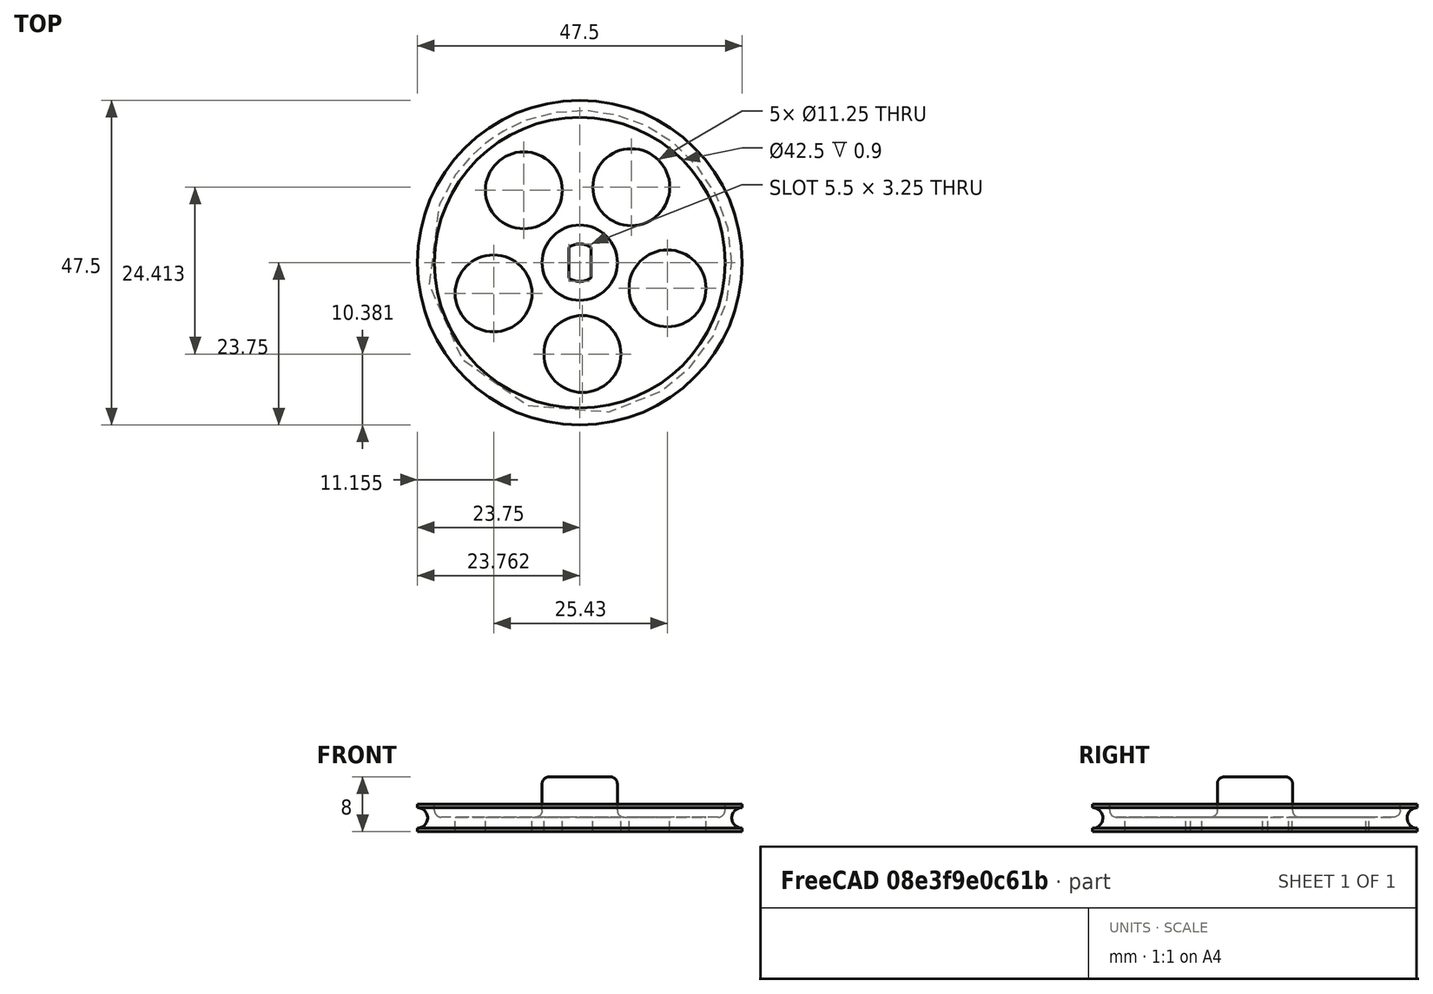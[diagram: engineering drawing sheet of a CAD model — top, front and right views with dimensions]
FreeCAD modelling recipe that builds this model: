
FCSTD DOCUMENT  (FreeCAD 0.16R6712 (Git))
Label: wheel_v02
License: All rights reserved
LicenseURL: http://en.wikipedia.org/wiki/All_rights_reserved
objects: Part::Cylinder×6, Part::Cut×5, Sketcher::SketchObject×1, Part::Torus×1, Part::Box×1, Part::MultiCommon×1, Part::FeaturePython×1, Drawing::FeaturePage×1, Part::MultiFuse×1, Spreadsheet::Sheet×1, PartDesign::Fillet×1
note: 18 computed .brp shape members not serialized (recipe doc carries the construction recipe); baked Part::Feature solids carry a one-line shape summary decoded from their .brp

FEATURE [Sketcher::SketchObject] Sketch
FEATURE [Part::Torus] Torus
  Angle1 = -180
  Angle2 = 180
  Angle3 = 360
  Placement = pos=(0,0,2) rot=(0,0,1;0rad)
  Radius1 = 23.75
  Radius2 = 1.5
  expr: Radius1 = data.wheel_diameter / 2
FEATURE [Part::Cylinder] Cylinder
  Angle = 360
  Height = 4
  Radius = 23.75
  expr: Height = data.rim_thickness
  expr: Radius = data.wheel_diameter / 2
FEATURE [Part::Cut] Cut  label="rim"
  Base = -> Cylinder
  Tool = -> Torus
FEATURE [Part::Cylinder] Cylinder001  label="hub"
  Angle = 360
  Height = 8
  Radius = 5.5
FEATURE [Part::Cylinder] Cylinder002  label="Cylinder001"
  Angle = 360
  Height = 12
  Radius = 2.75
FEATURE [Part::Box] Box  label="Cube"
  Height = 12
  Length = 3.25
  Placement = pos=(-1.6125,-6,0) rot=(0,0,1;0rad)
  Width = 12
FEATURE [Part::MultiCommon] Common  label="shaft"
  Shapes = -> [Box,Cylinder002]
FEATURE [Part::Cylinder] Cylinder003  label="setscrew"
  Angle = 360
  Height = 20
  Placement = pos=(-10,0,15) rot=(0,1,0;1.5708rad)
  Radius = 1.5
  expr: Placement.Base.z = data.setscrewZ
FEATURE [Part::Cylinder] Cylinder004  label="spoke"
  Angle = 360
  Height = 20
  Placement = pos=(13.375,0,0) rot=(0,0,1;0rad)
  Radius = 5.625
  expr: Radius = (data.wheel_diameter / 2 - 5.5mm) / 2 - 3.5mm
  expr: Placement.Base.x = (data.wheel_diameter / 2 - 2.5mm) / 2 + 2.75mm
FEATURE [Part::FeaturePython] Array  # Draft array (typed FeaturePython)
  Angle = 360
  ArrayType = 1
  Axis = (0,0,1)
  Base = -> Cylinder004
  Center = (0,0,0)
  Fuse = false
  IntervalAxis = (0,0,0)
  IntervalX = (1,0,0)
  IntervalY = (0,1,0)
  IntervalZ = (0,0,0)
  NumberPolar = 5
  NumberX = 1
  NumberY = 2
  NumberZ = 1
  Placement = pos=(0,0,0) rot=(0,0,1;2.22812rad)
  expr: NumberPolar = data.spokes
FEATURE [Drawing::FeaturePage] Page
  EditableTexts = AUTHOR NAME | CREATION DATE | SUPERVISOR NAME | CHECK DATE | SCALE | WEIGHT | NUMBER | SHEET | TITLE | SUBTITLE
FEATURE [Part::Cylinder] Cylinder005  label="Cylinder002"
  Angle = 360
  Height = 10
  Placement = pos=(0,0,2.1) rot=(0,0,1;0rad)
  Radius = 21.25
  expr: Radius = data.wheel_diameter / 2 - 2.5mm
FEATURE [Part::Cut] Cut002
  Base = -> Cut
  Tool = -> Cylinder005
FEATURE [Part::MultiFuse] Fusion
  Shapes = -> [Cylinder001,Cut002]
FEATURE [Part::Cut] Cut003
  Base = -> Fusion
  Tool = -> Common
FEATURE [Part::Cut] Cut004
  Base = -> Cut003
  Tool = -> Cylinder003
FEATURE [Part::Cut] Cut005
  Base = -> Cut004
  Tool = -> Array
FEATURE [Spreadsheet::Sheet] Spreadsheet  label="data"
  cells = A3=wheel_diameter; B3(wheel_diameter)==47.5mm; A4=rim_thickness; B4(rim_thickness)==4mm; A5=spokes; B5(spokes)=5; A6=setscrewZ; B6(setscrewZ)==15mm; C6=5mm to show, 15mm to hide
FEATURE [PartDesign::Fillet] Fillet
  Base = -> Cut005 [Edge16,Edge7,Edge1]
  Radius = 1
